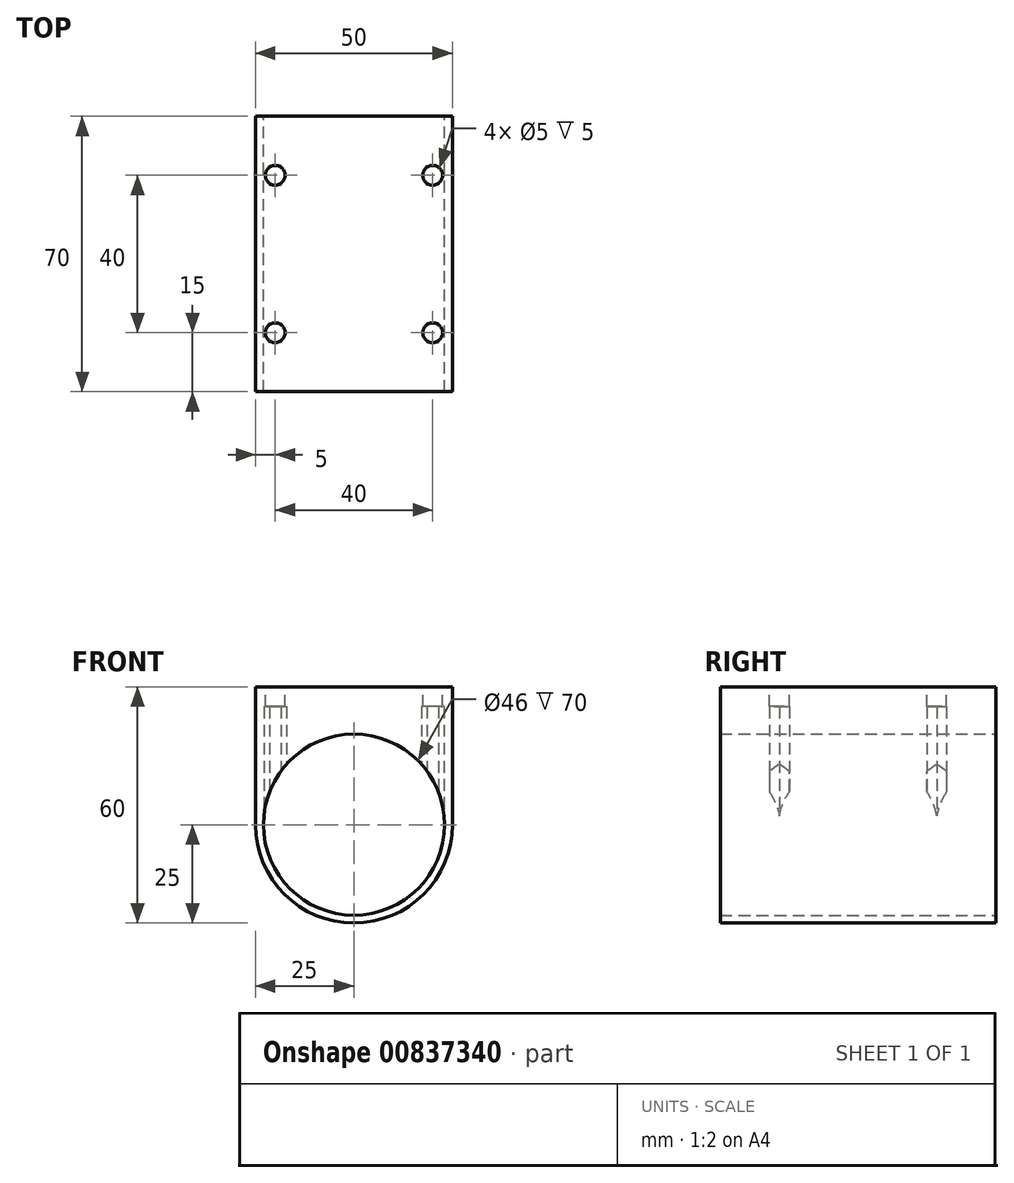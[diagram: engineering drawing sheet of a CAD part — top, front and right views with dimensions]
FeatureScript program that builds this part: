
annotation { "Feature Type Name" : "Feature", "Feature Type Description" : "" }
export const myFeature = defineFeature(function(context is Context, id is Id, definition is map)
    precondition{}
    {
        {
            var Q0;
            Q0=qCreatedBy(makeId("Front.planeOp"),FACE);
            var sketch = newSketch(context, id + "F0", { "sketchPlane" : qUnion([Q0])});
            skCircle(sketch, "E0", {"center": v(0, 0) * mm, "radius": 25 * mm});
            skLineSegment(sketch, "E1.bottom", {"start": v(-25, 0) * mm, "end": v(25, 0) * mm});
            skLineSegment(sketch, "E1.top", {"start": v(-25, 35) * mm, "end": v(25, 35) * mm});
            skLineSegment(sketch, "E1.left", {"start": v(-25, 0) * mm, "end": v(-25, 35) * mm});
            skLineSegment(sketch, "E1.right", {"start": v(25, 0) * mm, "end": v(25, 35) * mm});
            skArc(sketch, "E2", {"start": v(-23, 0) * mm, "mid": v(0, -23) * mm, "end": v(23, 0) * mm});
            skArc(sketch, "E3.MirrorCS", {"start": v(-23, 0) * mm, "mid": v(0, 23) * mm, "end": v(23, 0) * mm});
            skSolve(sketch);
        }
        {
            var Q0;
            Q0=makeQuery(id+"F0.imprint","IMPRINT",FACE,{"disambiguationData":[TD([[makeQuery(id+"F0.imprint","IMPRINT",EDGE,{"derivedFrom":sQuery(id+"F0.wireOp",EDGE,"E1.top")}),-1.0]])]});
            var Q1;
            {var subQ0=sQuery(id+"F0.wireOp",EDGE,"E1.bottom");Q1=makeQuery(id+"F0.imprint","IMPRINT",FACE,{"disambiguationData":[TD([[makeQuery(id+"F0.imprint","IMPRINT",EDGE,{"derivedFrom":subQ0}),1.0]])]});}
            extrude(context, id + "F1", {"entities" : qUnion([Q0, Q1]), "endBound" : BoundingType.SYMMETRIC, "depth" : 70 * mm, "offsetDistance" : 25 * mm});
        }
        {
            var Q0;
            Q0=makeQuery(id+"F1.opExtrude","SWEPT_FACE",FACE,{"disambiguationData":[OSD([sQuery(id+"F0.wireOp",EDGE,"E1.top")])]});
            var sketch = newSketch(context, id + "F2", { "sketchPlane" : qUnion([Q0])});
            skCircle(sketch, "E4", {"center": v(20, 20) * mm, "radius": 2.5 * mm});
            skCircle(sketch, "E5.MirrorC", {"center": v(-20, 20) * mm, "radius": 2.5 * mm});
            skCircle(sketch, "E6.MirrorC", {"center": v(-20, -20) * mm, "radius": 2.5 * mm});
            skCircle(sketch, "E7.MirrorC", {"center": v(20, -20) * mm, "radius": 2.5 * mm});
            skSolve(sketch);
        }
        {
            var Q0;
            Q0 = qSketchRegion(id + "F2", true);
            extrude(context, id + "F3", {"entities" : qUnion([Q0]), "operationType" : NewBodyOperationType.REMOVE, "endBound" : BoundingType.THROUGH_ALL, "oppositeDirection" : true, "depth" : 25 * mm, "offsetDistance" : 25 * mm});
        }
        {
            var Q0;
            {var subQ4=sQuery(id+"F0.wireOp",EDGE,"E2");Q0=makeQuery(id+"F0.imprint","IMPRINT",FACE,{"disambiguationData":[TD([[makeQuery(id+"F0.imprint","IMPRINT",EDGE,{"derivedFrom":subQ4}),-1.0]])]});}
            extrude(context, id + "F4", {"entities" : qUnion([Q0]), "operationType" : NewBodyOperationType.ADD, "endBound" : BoundingType.SYMMETRIC, "depth" : 70 * mm, "offsetDistance" : 25 * mm});
        }
        {
            var Q0;
            Q0=qCreatedBy(makeId("Top.planeOp"),FACE);
            var sketch = newSketch(context, id + "F5", { "sketchPlane" : qUnion([Q0])});
            skCircle(sketch, "E8.cCircle", {"center": v(-20, -20) * mm, "radius": 2.5 * mm, "construction": true});
            skLineSegment(sketch, "E8.0", {"start": v(-18.56, -17.5) * mm, "end": v(-17.11, -20) * mm});
            skLineSegment(sketch, "E8.1", {"start": v(-17.11, -20) * mm, "end": v(-18.56, -22.5) * mm});
            skLineSegment(sketch, "E8.2", {"start": v(-18.56, -22.5) * mm, "end": v(-21.44, -22.5) * mm});
            skLineSegment(sketch, "E8.3", {"start": v(-21.44, -22.5) * mm, "end": v(-22.89, -20) * mm});
            skLineSegment(sketch, "E8.4", {"start": v(-22.89, -20) * mm, "end": v(-21.44, -17.5) * mm});
            skLineSegment(sketch, "E8.5", {"start": v(-21.44, -17.5) * mm, "end": v(-18.56, -17.5) * mm});
            skPoint(sketch, "E8.0.midPoint", {"position": v(-17.83, -18.75) * mm});
            skLineSegment(sketch, "E9.MirrorCS", {"start": v(18.56, -17.5) * mm, "end": v(17.11, -20) * mm});
            skLineSegment(sketch, "E10.MirrorCS", {"start": v(22.89, -20) * mm, "end": v(21.44, -17.5) * mm});
            skLineSegment(sketch, "E11.MirrorCS", {"start": v(21.44, -17.5) * mm, "end": v(18.56, -17.5) * mm});
            skLineSegment(sketch, "E12.MirrorCS", {"start": v(21.44, -22.5) * mm, "end": v(22.89, -20) * mm});
            skPoint(sketch, "E13.MirrorP", {"position": v(17.83, -18.75) * mm});
            skLineSegment(sketch, "E14.MirrorCS", {"start": v(17.11, -20) * mm, "end": v(18.56, -22.5) * mm});
            skLineSegment(sketch, "E15.MirrorCS", {"start": v(18.56, -22.5) * mm, "end": v(21.44, -22.5) * mm});
            skCircle(sketch, "E16.MirrorC", {"center": v(20, -20) * mm, "radius": 2.5 * mm, "construction": true});
            skLineSegment(sketch, "E17.MirrorCS", {"start": v(-18.56, 17.5) * mm, "end": v(-17.11, 20) * mm});
            skCircle(sketch, "E18.MirrorC", {"center": v(-20, 20) * mm, "radius": 2.5 * mm, "construction": true});
            skLineSegment(sketch, "E19.MirrorCS", {"start": v(-21.44, 17.5) * mm, "end": v(-18.56, 17.5) * mm});
            skLineSegment(sketch, "E20.MirrorCS", {"start": v(-22.89, 20) * mm, "end": v(-21.44, 17.5) * mm});
            skPoint(sketch, "E21.MirrorP", {"position": v(-17.83, 18.75) * mm});
            skLineSegment(sketch, "E22.MirrorCS", {"start": v(-17.11, 20) * mm, "end": v(-18.56, 22.5) * mm});
            skLineSegment(sketch, "E23.MirrorCS", {"start": v(-18.56, 22.5) * mm, "end": v(-21.44, 22.5) * mm});
            skLineSegment(sketch, "E24.MirrorCS", {"start": v(-21.44, 22.5) * mm, "end": v(-22.89, 20) * mm});
            skLineSegment(sketch, "E25.MirrorCS", {"start": v(18.56, 17.5) * mm, "end": v(17.11, 20) * mm});
            skLineSegment(sketch, "E26.MirrorCS", {"start": v(21.44, 17.5) * mm, "end": v(18.56, 17.5) * mm});
            skLineSegment(sketch, "E27.MirrorCS", {"start": v(18.56, 22.5) * mm, "end": v(21.44, 22.5) * mm});
            skCircle(sketch, "E28.MirrorC", {"center": v(20, 20) * mm, "radius": 2.5 * mm, "construction": true});
            skPoint(sketch, "E29.MirrorP", {"position": v(17.83, 18.75) * mm});
            skLineSegment(sketch, "E30.MirrorCS", {"start": v(22.89, 20) * mm, "end": v(21.44, 17.5) * mm});
            skLineSegment(sketch, "E31.MirrorCS", {"start": v(21.44, 22.5) * mm, "end": v(22.89, 20) * mm});
            skLineSegment(sketch, "E32.MirrorCS", {"start": v(17.11, 20) * mm, "end": v(18.56, 22.5) * mm});
            skSolve(sketch);
        }
        {
            var Q0;
            Q0 = qSketchRegion(id + "F5", true);
            extrude(context, id + "F6", {"entities" : qUnion([Q0]), "operationType" : NewBodyOperationType.REMOVE, "depth" : 30 * mm, "offsetDistance" : 25 * mm});
        }
    });
